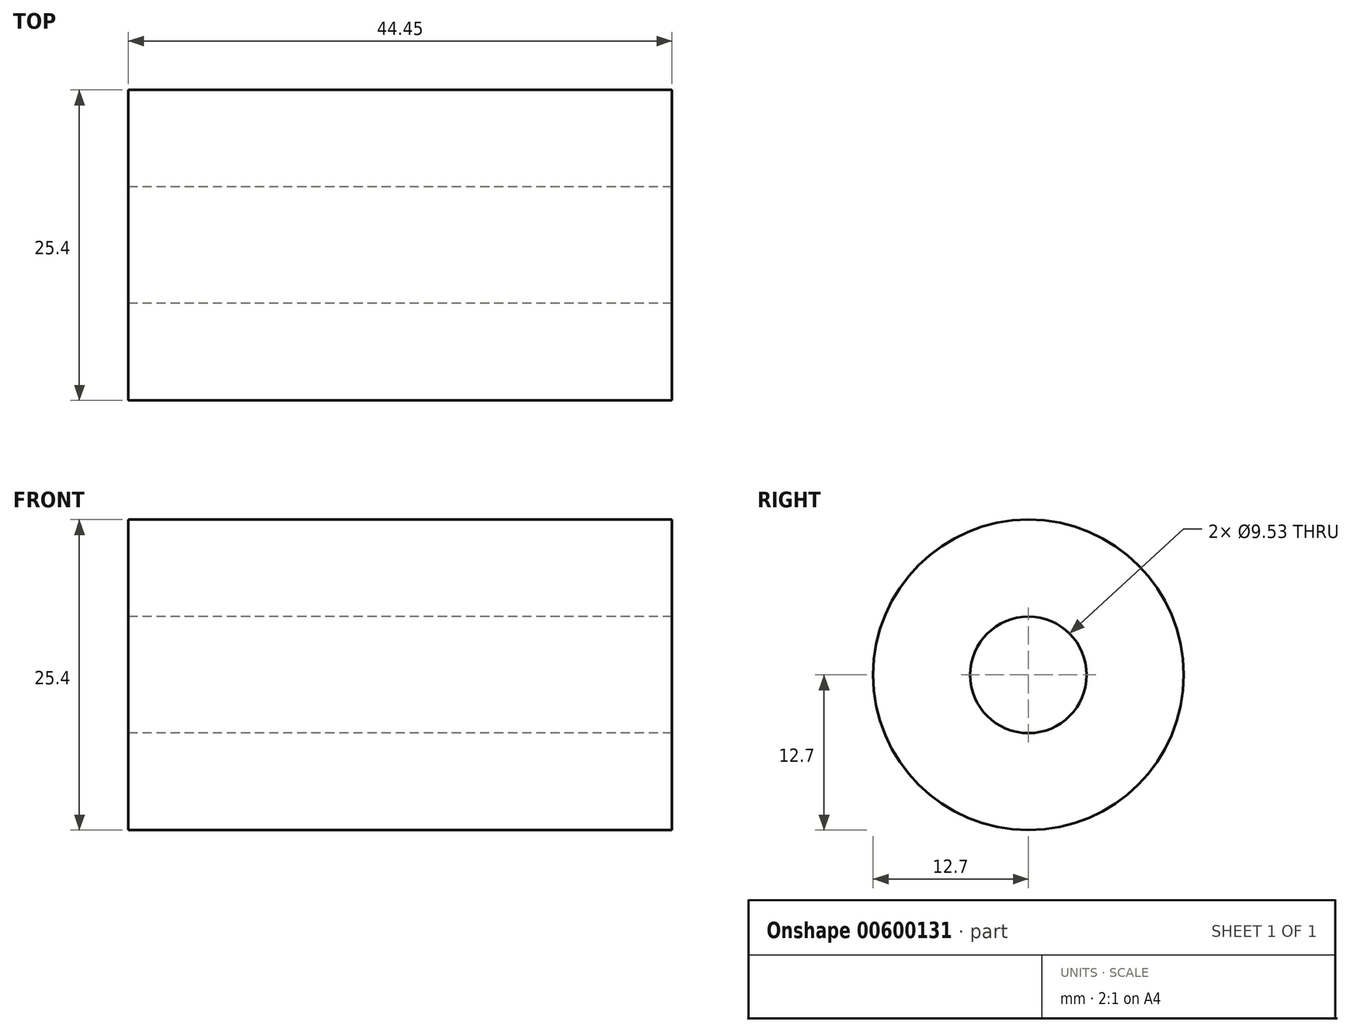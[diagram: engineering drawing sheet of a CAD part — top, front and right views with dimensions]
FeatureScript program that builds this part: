
annotation { "Feature Type Name" : "Feature", "Feature Type Description" : "" }
export const myFeature = defineFeature(function(context is Context, id is Id, definition is map)
    precondition{}
    {
        {
            var Q0;
            Q0=qCreatedBy(makeId("Right.planeOp"),FACE);
            var sketch = newSketch(context, id + "F0", { "sketchPlane" : qUnion([Q0])});
            skCircle(sketch, "E0", {"center": v(0, 0) * mm, "radius": 12.7 * mm});
            skCircle(sketch, "E1", {"center": v(0, 0) * mm, "radius": 4.76 * mm});
            skSolve(sketch);
        }
        {
            var Q0;
            Q0=qSketchRegion(id+"F0",true);
            extrude(context, id + "F1", {"entities" : qUnion([Q0]), "depth" : 44.45 * mm});
        }
    });
